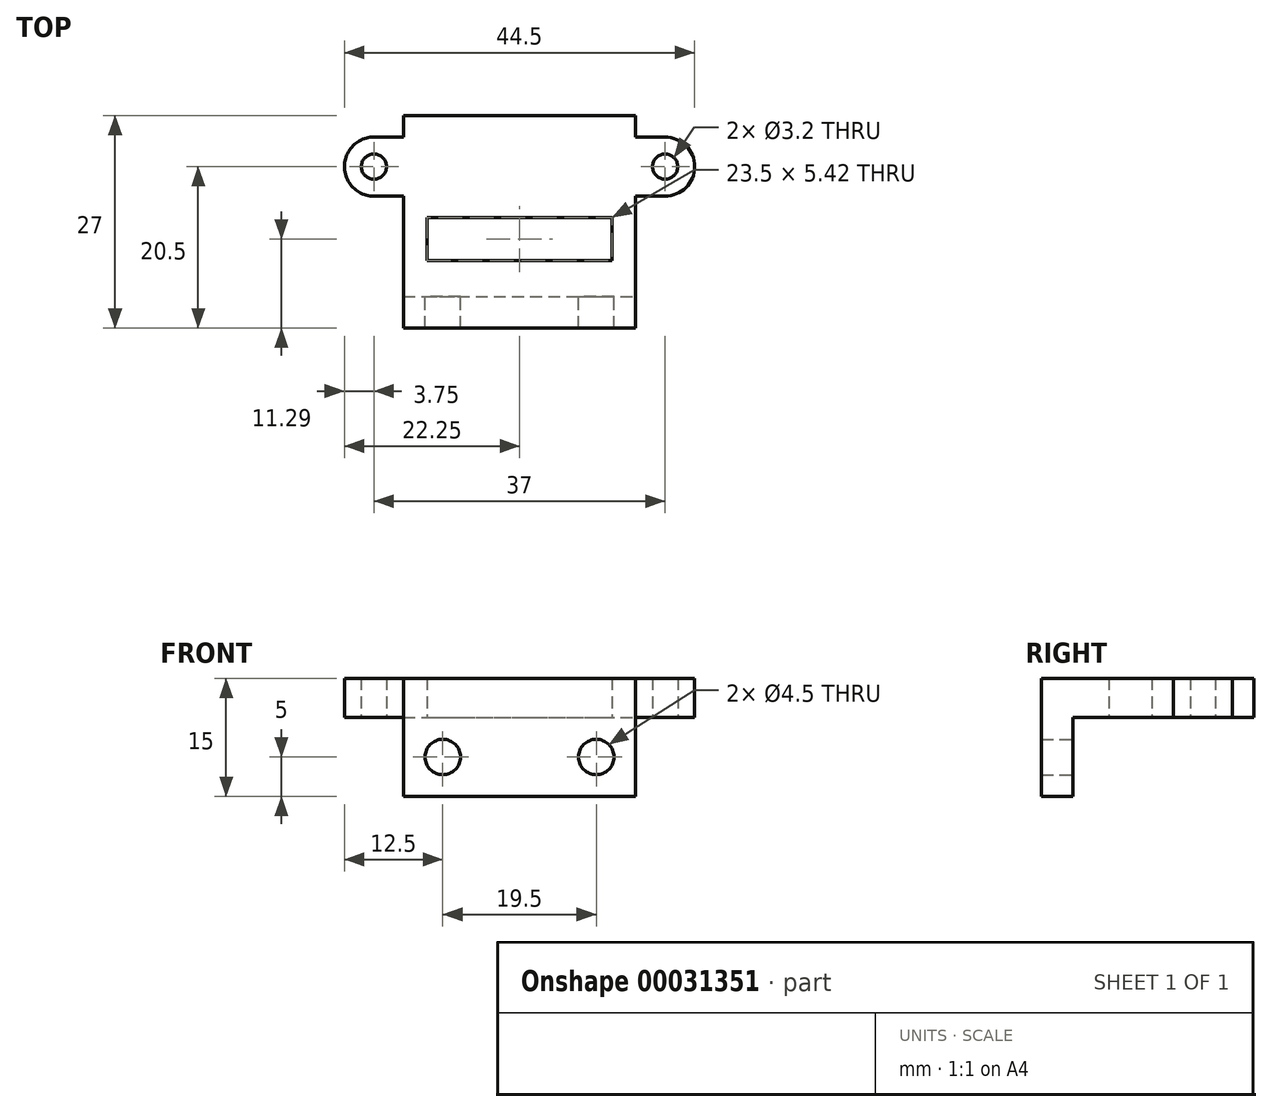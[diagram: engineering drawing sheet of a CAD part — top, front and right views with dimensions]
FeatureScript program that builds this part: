
annotation { "Feature Type Name" : "Feature", "Feature Type Description" : "" }
export const myFeature = defineFeature(function(context is Context, id is Id, definition is map)
    precondition{}
    {
        {
            var Q0;
            Q0=qCreatedBy(makeId("Top.planeOp"),FACE);
            var sketch = newSketch(context, id + "F0", { "sketchPlane" : qUnion([Q0])});
            skLineSegment(sketch, "E0.bottom", {"start": v(-14.75, 6.5) * mm, "end": v(14.75, 6.5) * mm});
            skLineSegment(sketch, "E0.top", {"start": v(-14.75, -6.5) * mm, "end": v(14.75, -6.5) * mm});
            skLineSegment(sketch, "E0.left", {"start": v(-14.75, 6.5) * mm, "end": v(-14.75, -6.5) * mm});
            skLineSegment(sketch, "E0.right", {"start": v(14.75, 6.5) * mm, "end": v(14.75, 3.75) * mm});
            skArc(sketch, "E1", {"start": v(18.5, -3.75) * mm, "mid": v(22.25, 0) * mm, "end": v(18.5, 3.75) * mm});
            skArc(sketch, "E2", {"start": v(-18.48, 3.75) * mm, "mid": v(-22.25, 0.01) * mm, "end": v(-18.5, -3.75) * mm});
            skLineSegment(sketch, "E3", {"start": v(-18.48, 3.75) * mm, "end": v(-14.75, 3.73) * mm});
            skLineSegment(sketch, "E4", {"start": v(-18.5, -3.75) * mm, "end": v(-14.75, -3.75) * mm});
            skLineSegment(sketch, "E5", {"start": v(18.5, 3.75) * mm, "end": v(14.75, 3.75) * mm});
            skLineSegment(sketch, "E6", {"start": v(18.5, -3.75) * mm, "end": v(14.75, -3.75) * mm});
            skLineSegment(sketch, "E7.trimOffspring", {"start": v(14.75, -3.75) * mm, "end": v(14.75, -6.5) * mm});
            skCircle(sketch, "E8", {"center": v(-18.5, 0) * mm, "radius": 1.6 * mm});
            skCircle(sketch, "E9", {"center": v(18.5, 0) * mm, "radius": 1.6 * mm});
            skSolve(sketch);
        }
        {
            var Q0;
            Q0 = qSketchRegion(id + "F0", true);
            extrude(context, id + "F1", {"entities" : qUnion([Q0]), "depth" : 5 * mm});
        }
        {
            var Q0;
            Q0=makeQuery(id+"F1.opExtrude","SWEPT_FACE",FACE,{"disambiguationData":[OSD([sQuery(id+"F0.wireOp",EDGE,"E0.top")])]});
            var sketch = newSketch(context, id + "F2", { "sketchPlane" : qUnion([Q0])});
            skLineSegment(sketch, "E10.bottom", {"start": v(-14.75, 5) * mm, "end": v(14.75, 5) * mm});
            skLineSegment(sketch, "E10.top", {"start": v(-14.75, 0) * mm, "end": v(14.75, 0) * mm});
            skLineSegment(sketch, "E10.left", {"start": v(-14.75, 5) * mm, "end": v(-14.75, 0) * mm});
            skLineSegment(sketch, "E10.right", {"start": v(14.75, 5) * mm, "end": v(14.75, 0) * mm});
            skSolve(sketch);
        }
        {
            var Q0;
            Q0 = qSketchRegion(id + "F2", true);
            extrude(context, id + "F3", {"entities" : qUnion([Q0]), "operationType" : NewBodyOperationType.ADD, "depth" : 10 * mm});
        }
        {
            var Q0;
            Q0=makeQuery(id+"F3.opExtrude","CAP_FACE",FACE,{"disambiguationData":[OSD([sQuery(id+"F2.wireOp",EDGE,"E10.bottom"),sQuery(id+"F2.wireOp",EDGE,"E10.top"),sQuery(id+"F2.wireOp",EDGE,"E10.left"),sQuery(id+"F2.wireOp",EDGE,"E10.right")])],"isStart":false});
            var sketch = newSketch(context, id + "F4", { "sketchPlane" : qUnion([Q0])});
            skLineSegment(sketch, "E11.bottom", {"start": v(-14.75, 5) * mm, "end": v(14.75, 5) * mm});
            skLineSegment(sketch, "E11.top", {"start": v(-14.75, -10) * mm, "end": v(14.75, -10) * mm});
            skLineSegment(sketch, "E11.left", {"start": v(-14.75, 5) * mm, "end": v(-14.75, -10) * mm});
            skLineSegment(sketch, "E11.right", {"start": v(14.75, 5) * mm, "end": v(14.75, -10) * mm});
            skSolve(sketch);
        }
        {
            var Q0;
            Q0 = qSketchRegion(id + "F4", true);
            extrude(context, id + "F5", {"entities" : qUnion([Q0]), "operationType" : NewBodyOperationType.ADD, "depth" : 4 * mm});
        }
        {
            var Q0;
            Q0=makeQuery(id+"F5.opExtrude","CAP_FACE",FACE,{"disambiguationData":[OSD([sQuery(id+"F4.wireOp",EDGE,"E11.bottom"),sQuery(id+"F4.wireOp",EDGE,"E11.top"),sQuery(id+"F4.wireOp",EDGE,"E11.left"),sQuery(id+"F4.wireOp",EDGE,"E11.right")])],"isStart":true});
            var sketch = newSketch(context, id + "F6", { "sketchPlane" : qUnion([Q0])});
            skCircle(sketch, "E12", {"center": v(-9.75, -5) * mm, "radius": 2.25 * mm});
            skCircle(sketch, "E13", {"center": v(9.75, -5) * mm, "radius": 2.25 * mm});
            skSolve(sketch);
        }
        {
            var Q0;
            Q0 = qSketchRegion(id + "F6", true);
            extrude(context, id + "F7", {"entities" : qUnion([Q0]), "operationType" : NewBodyOperationType.REMOVE, "oppositeDirection" : true, "depth" : 25 * mm});
        }
        {
            var Q0;
            Q0=makeQuery(id+"F3.boolean.opBoolean","MERGE",FACE,{"derivedFrom":[makeQuery(id+"F1.opExtrude","CAP_FACE",FACE,{"disambiguationData":[OSD([sQuery(id+"F0.wireOp",EDGE,"E0.bottom"),sQuery(id+"F0.wireOp",EDGE,"E0.top"),sQuery(id+"F0.wireOp",EDGE,"E0.left"),sQuery(id+"F0.wireOp",EDGE,"E0.right"),sQuery(id+"F0.wireOp",EDGE,"E1"),sQuery(id+"F0.wireOp",EDGE,"E2"),sQuery(id+"F0.wireOp",EDGE,"E3"),sQuery(id+"F0.wireOp",EDGE,"E4"),sQuery(id+"F0.wireOp",EDGE,"E5"),sQuery(id+"F0.wireOp",EDGE,"E6"),sQuery(id+"F0.wireOp",EDGE,"E7.trimOffspring"),sQuery(id+"F0.wireOp",EDGE,"E8"),sQuery(id+"F0.wireOp",EDGE,"E9")])],"isStart":true}),makeQuery(id+"F3.opExtrude","SWEPT_FACE",FACE,{"disambiguationData":[OSD([sQuery(id+"F2.wireOp",EDGE,"E10.top")])]})]});
            var sketch = newSketch(context, id + "F8", { "sketchPlane" : qUnion([Q0])});
            skLineSegment(sketch, "E14.bottom", {"start": v(-11.75, 11.92) * mm, "end": v(11.75, 11.92) * mm});
            skLineSegment(sketch, "E14.top", {"start": v(-11.75, 6.5) * mm, "end": v(11.75, 6.5) * mm});
            skLineSegment(sketch, "E14.left", {"start": v(-11.75, 11.92) * mm, "end": v(-11.75, 6.5) * mm});
            skLineSegment(sketch, "E14.right", {"start": v(11.75, 11.92) * mm, "end": v(11.75, 6.5) * mm});
            skSolve(sketch);
        }
        {
            var Q0;
            Q0 = qSketchRegion(id + "F8", true);
            extrude(context, id + "F9", {"entities" : qUnion([Q0]), "operationType" : NewBodyOperationType.REMOVE, "oppositeDirection" : true, "depth" : 25 * mm});
        }
    });
